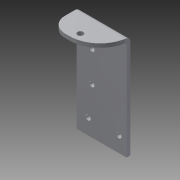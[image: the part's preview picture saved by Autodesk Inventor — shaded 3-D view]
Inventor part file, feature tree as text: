
AUTODESK INVENTOR PART (.ipt)
format: ipt  version: 2014 (Build 180170000, 170)  size: 185,856 bytes
history: native  units: in
note: dims shown in document units (in); Inventor stores cm internally (conversion verified against a paired STEP export)
features: sheet_metal_op x4, other x4, sketch x2, fillet x1
ambient origin geometry x8: Origin, YZ Plane, XZ Plane, XY Plane, X Axis, Y Axis, Z Axis, Center Point
bodies: Solid1 (feature_tree)
feature tree (11):
  sheet_metal_op  "Face1"
  sheet_metal_op  "Flange1"
  fillet  "Fillet3"  Radius=1.625in
  sketch  "Sketch1"  dims[d1=4.1875in]
  other  "Plate1"
  sketch  "Sketch2"  dims[d2=0.163in d4=0.7874in d6=1.0in d7=0.3937in d9=1.0in d11=0.125in d12=0.125in d13=0.0625in d14=0.25in d15=0.125in d16=1.0in d17=90.0deg d18=0.05in d19=0.5in d20=0.125in d21=0.125in d22=0.5in d28=0.187in d29=0.25in d34=0.75in d36=0.25in d38=0.5in d39=1.5in d40=1.1811in d42=1.0in d43=0.3937in d45=1.0in d47=0.125in d48=0.25in d49=0.25in d50=0.375in d51=0.125in d52=0.0in d53=0.25in]
  other  "Plate2"
  sheet_metal_op  "Bend1"
  sheet_metal_op  "Corner1"
  other  "Cut3"
  other  "Definition1"
